# Revit family: DSFI-45-IS-AG_2014
name_source: partatom
category: Specialty Equipment
revit_build: Autodesk Revit 2014 (Build: 20130308_1515(x64)
units: mm (PartAtom-declared; Revit-internal decimal feet)

## types (1)
- 45 IS
    Bumper = Extruded PVC - 701 Black
    Case = Textured Sheet Metal (Steel Painted) - 701 Black
    Case Interior - Back Panel = Sheet Metal (Steel Painted) - 701 Black
    Case Interior - Side Panel = Sheet Metal (Steel Painted) - 701 Black
    Case Weight = 0.00 lbf
    Close Off Panel = Textured Sheet Metal (Steel Painted) - 701 Black
    Cutsheet URL = http://www.hussmann.com
    Depth = 35"
    Description = Medium Depth Service Merchandiser for Fresh Seafood Applications
    Door Frame = Stainless Steel
    End Weight = 0.00 lbf
    Ends = Textured Sheet Metal (Steel Painted) - 701 Black
    Glazing = Glass
    Height = 45 5/8"
    Manufacturer = Hussmann Corporation
    Manufacturer Disclaimer = The information in this file is not intended to be an exact representation of the corresponding Hussmann product.  Further, we reserve the right to change or revise specifications and product design in connection with any feature of our products. Such changes do not entitle the buyer to corresponding changes, improvements, additions, or replacements for equipment previously sold or shipped.
    Model = DSFI 45 IS
    Model URL = http://www.hussmann.com
    Note from Manufacturer = This model only comes in this size.
    Refrig. Liquid = Liquid
    Refrig. Suction = Suction
    Refrigeration Lines Liquid = 3/8"
    Refrigeration Lines Suction = 5/8"
    Revit Family Date = 08/11/2015
    Shelves = Sheet Metal (Steel Painted) - 701 Black
    Splashguard = Stainless Steel
    Total Weight = 0.00 lbf
    Trim = Stainless Steel
    Type Comments = Service / Self Service Seafood
    URL = www.hussmann.com
    Waste Drain = 1 1/2"
    Width = 26 3/4"

## geometry (parser evidence)
native form markers: Blend x4, Sweep x3
no freeform markers — native parametric forms only
